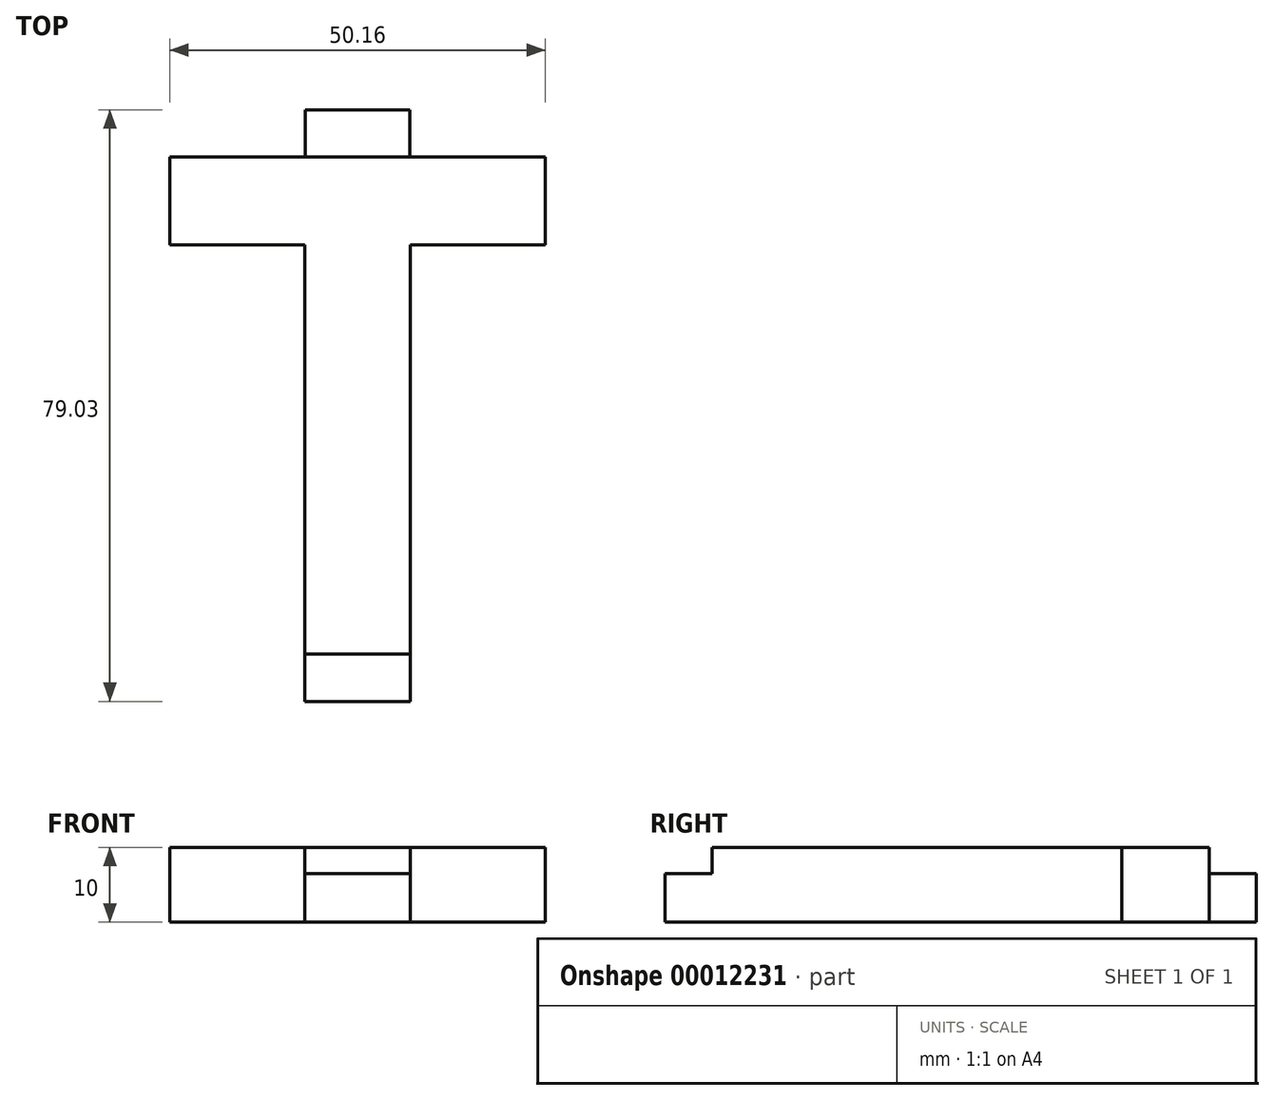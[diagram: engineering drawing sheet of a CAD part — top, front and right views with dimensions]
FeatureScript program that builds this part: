
annotation { "Feature Type Name" : "Feature", "Feature Type Description" : "" }
export const myFeature = defineFeature(function(context is Context, id is Id, definition is map)
    precondition{}
    {
        {
            var Q0;
            Q0=qCreatedBy(makeId("Top.planeOp"),FACE);
            var sketch = newSketch(context, id + "F0", { "sketchPlane" : qUnion([Q0])});
            skText(sketch, "E0", { "text": "T", "fontName": "OpenSans-Bold.ttf"});
            const initialGuessF0  = {"E0": [-0.05202, 0, 1, 0, 0.067]};
            skSetInitialGuess(sketch, initialGuessF0);
            skSolve(sketch);
        }
        {
            var Q0;
            Q0=makeQuery(id+"F0.imprint","IMPRINT",FACE,{"disambiguationData":[TD([[makeQuery(id+"F0.imprint","IMPRINT",EDGE,{"derivedFrom":sQuery(id+"F0.wireOp",EDGE,"E0.sketch_text.stroke-0")}),-1.0]])]});
            extrude(context, id + "F1", {"entities" : qUnion([Q0]), "depth" : 10 * mm});
        }
        {
            var Q0;
            Q0=makeQuery(id+"F1.opExtrude","SWEPT_FACE",FACE,{"disambiguationData":[OSD([sQuery(id+"F0.wireOp",EDGE,"E0.sketch_text.stroke-0")])]});
            var sketch = newSketch(context, id + "F2", { "sketchPlane" : qUnion([Q0])});
            skLineSegment(sketch, "E1.0.0", {"start": v(-32.12, 0) * mm, "end": v(-18.03, 0) * mm});
            skLineSegment(sketch, "E1.0.1", {"start": v(-18.03, 0) * mm, "end": v(-18.03, 10) * mm});
            skLineSegment(sketch, "E1.0.2", {"start": v(-18.03, 10) * mm, "end": v(-32.12, 10) * mm});
            skLineSegment(sketch, "E1.0.3", {"start": v(-32.12, 10) * mm, "end": v(-32.12, 0) * mm});
            skLineSegment(sketch, "E2.top", {"start": v(-32.12, 6.5) * mm, "end": v(-18.03, 6.5) * mm});
            skLineSegment(sketch, "E2.left", {"start": v(-32.12, 0) * mm, "end": v(-32.12, 6.5) * mm});
            skLineSegment(sketch, "E2.right", {"start": v(-18.03, 0) * mm, "end": v(-18.03, 6.5) * mm});
            skSolve(sketch);
        }
        {
            var Q0;
            Q0=makeQuery(id+"F2.imprint","IMPRINT",FACE,{"disambiguationData":[TD([[makeQuery(id+"F2.imprint","IMPRINT",EDGE,{"derivedFrom":sQuery(id+"F2.wireOp",EDGE,"E1.0.0")}),-1.0]])]});
            extrude(context, id + "F3", {"entities" : qUnion([Q0]), "operationType" : NewBodyOperationType.ADD, "depth" : 6.3 * mm});
        }
        {
            var Q0;
            Q0=makeQuery(id+"F1.opExtrude","SWEPT_FACE",FACE,{"disambiguationData":[OSD([sQuery(id+"F0.wireOp",EDGE,"E0.sketch_text.stroke-4")])]});
            var sketch = newSketch(context, id + "F4", { "sketchPlane" : qUnion([Q0])});
            skLineSegment(sketch, "E3.0.0", {"start": v(0, 0) * mm, "end": v(50.16, 0) * mm, "construction": true});
            skLineSegment(sketch, "E3.0.1", {"start": v(50.16, 0) * mm, "end": v(50.16, 10) * mm});
            skLineSegment(sketch, "E3.0.2", {"start": v(50.16, 10) * mm, "end": v(0, 10) * mm});
            skLineSegment(sketch, "E3.0.3", {"start": v(0, 10) * mm, "end": v(0, 0) * mm});
            skLineSegment(sketch, "E4.bottom", {"start": v(18.08, 0) * mm, "end": v(32.08, 0) * mm});
            skLineSegment(sketch, "E4.top", {"start": v(18.08, 6.5) * mm, "end": v(32.08, 6.5) * mm});
            skLineSegment(sketch, "E4.left", {"start": v(18.08, 0) * mm, "end": v(18.08, 6.5) * mm});
            skLineSegment(sketch, "E4.right", {"start": v(32.08, 0) * mm, "end": v(32.08, 6.5) * mm});
            skLineSegment(sketch, "E5", {"start": v(25.08, 0) * mm, "end": v(25.08, 1.26) * mm, "construction": true});
            skLineSegment(sketch, "E6", {"start": v(25.08, 0) * mm, "end": v(25.08, 1.9) * mm, "construction": true});
            skSolve(sketch);
        }
        {
            var Q0;
            Q0=makeQuery(id+"F4.imprint","IMPRINT",FACE,{"disambiguationData":[TD([[makeQuery(id+"F4.imprint","IMPRINT",EDGE,{"derivedFrom":sQuery(id+"F4.wireOp",EDGE,"E4.bottom")}),-1.0]])]});
            extrude(context, id + "F5", {"entities" : qUnion([Q0]), "operationType" : NewBodyOperationType.ADD, "depth" : 6.3 * mm});
        }
    });
